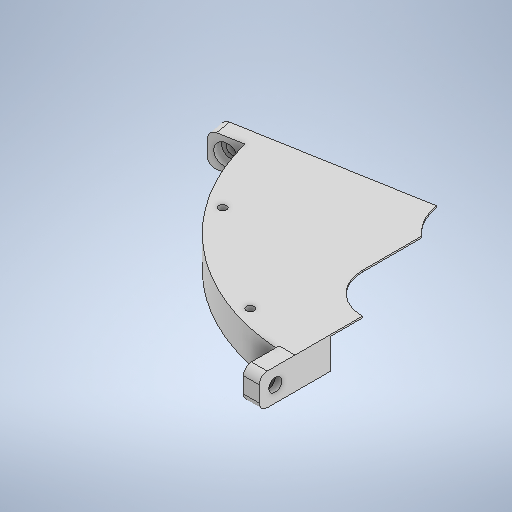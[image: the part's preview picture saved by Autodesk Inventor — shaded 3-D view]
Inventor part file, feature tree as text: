
AUTODESK INVENTOR PART (.ipt)
format: ipt  version: 2025 (Build 290162000, 162)  size: 404,480 bytes
history: native  units: in
note: dims shown in document units (in); Inventor stores cm internally (conversion verified against a paired STEP export)
features: sketch x15, extrude x11, hole x3
ambient origin geometry x8: Origin, YZ Plane, XZ Plane, XY Plane, X Axis, Y Axis, Z Axis, Center Point
bodies: Solid1 (feature_tree)
feature tree (29):
  extrude  "Extrusion1"  Depth=8.6614in
  extrude  "Extrusion2"  Depth=1.4173in
  extrude  "Extrusion3"  TaperAngle=0.0deg  [1 undecoded]
  extrude  "Extrusion4"  Depth=0.7874in
  hole  "Hole1"  [1 undecoded]
  extrude  "Extrusion5"  Depth=10.0394in
  extrude  "Extrusion6"  Depth=0.1575in TaperAngle=360.0deg
  extrude  "Extrusion7"  Depth=0.5906in TaperAngle=0.0deg
  extrude  "Extrusion8"  Depth=0.0394in TaperAngle=0.0deg
  extrude  "Extrusion9"  TaperAngle=0.0deg  [1 undecoded]
  extrude  "Extrusion10"  Depth=0.7874in
  hole  "Hole2"  [1 undecoded]
  extrude  "Extrusion11"  Depth=0.8858in
  hole  "Hole3"  [1 undecoded]
  sketch  "Sketch1"  dims[d0=10.6299in d1=8.6614in]
  sketch  "Sketch2"  dims[d5=0.1969in d6=0.0in d7=0.0in]
  sketch  "Sketch3"  dims[d8=0.7874in d9=0.0in d10=2.7559in]
  sketch  "Sketch4"  dims[d11=0.7874in d12=7.874in]
  sketch  "Sketch5"  dims[d13=0.0in d14=0.0in d15=10.0394in]
  sketch  "Sketch Circular Pattern1"  dims[d2=2.1654in d3=0.0in d4=1.4173in]
  sketch  "Sketch6"  dims[d16=0.1575in d17=3.937in d19=360.0deg]
  sketch  "Sketch7"  dims[d21=0.1969in d22=0.3937in d23=0.4094in d24=0.0787in d25=90.0deg d26=0.315in d27=0.8108in d28=0.5906in d29=0.0in]
  sketch  "Sketch8"  dims[d30=2.9528in d33=0.0394in d34=0.0in d38=0.5512in d39=0.0in]
  sketch  "Sketch9"  dims[d40=0.5497in d41=0.0in d42=0.0in]
  sketch  "Sketch10"  dims[d43=0.8858in d44=0.7874in]
  sketch  "Sketch11"  dims[d45=0.7874in d46=0.1969in]
  sketch  "Sketch12"  dims[d48=0.3937in d49=0.0in d50=0.8858in]
  sketch  "Sketch13"  dims[d51=0.7874in d52=0.7874in]
  sketch  "Sketch14"  dims[d53=0.1969in d56=0.3937in d57=0.0in d58=0.3937in d59=0.3937in d60=0.3228in d61=0.2362in d62=0.5197in d63=0.2362in d64=90.0deg d65=0.315in d66=0.8108in d67=0.3937in d68=0.3937in d69=0.5197in d70=0.2362in d71=0.0in d72=0.3937in d73=0.3937in d74=0.3228in d75=0.2362in d76=0.5197in d77=0.2362in d78=90.0deg d79=0.315in d80=0.8108in]
note: 5 required parameter values undecoded (feature->parameter linkage not recoverable at this tier; creation-order binding heuristic only, values carry confidence <= 0.55)
